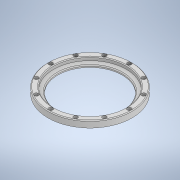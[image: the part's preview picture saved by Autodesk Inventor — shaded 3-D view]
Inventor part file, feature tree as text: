
AUTODESK INVENTOR PART (.ipt)
format: ipt  version: 2021 (Build 250183000, 183)  size: 185,344 bytes
history: native  units: mm
features: sketch x2, revolve x1, extrude x1, pattern_circular x1, chamfer x1
ambient origin geometry x8: Origin, YZ Plane, XZ Plane, XY Plane, X Axis, Y Axis, Z Axis, Center Point
bodies: Solid1 (feature_tree)
feature tree (6):
  revolve  "Revolution1"  [1 undecoded]
  extrude  "Extrusion1"  Depth=103.0mm
  pattern_circular  "Circular Pattern1"  [2 undecoded]
  chamfer  "Chamfer1"  Distance=15.0mm
  sketch  "Sketch1"  dims[d0=15.0deg d1=95.2mm]
  sketch  "Sketch2"  dims[d3=84.5mm d4=5.0mm d5=12.0mm d7=15.0mm d8=90.0deg d9=10.5mm d10=103.0mm d11=0.0mm d12=0.0mm d13=120.0mm d14=360.0deg d16=2.0mm d17=2.0mm d18=45.0deg]
note: 3 required parameter values undecoded (feature->parameter linkage not recoverable at this tier; creation-order binding heuristic only, values carry confidence <= 0.55)